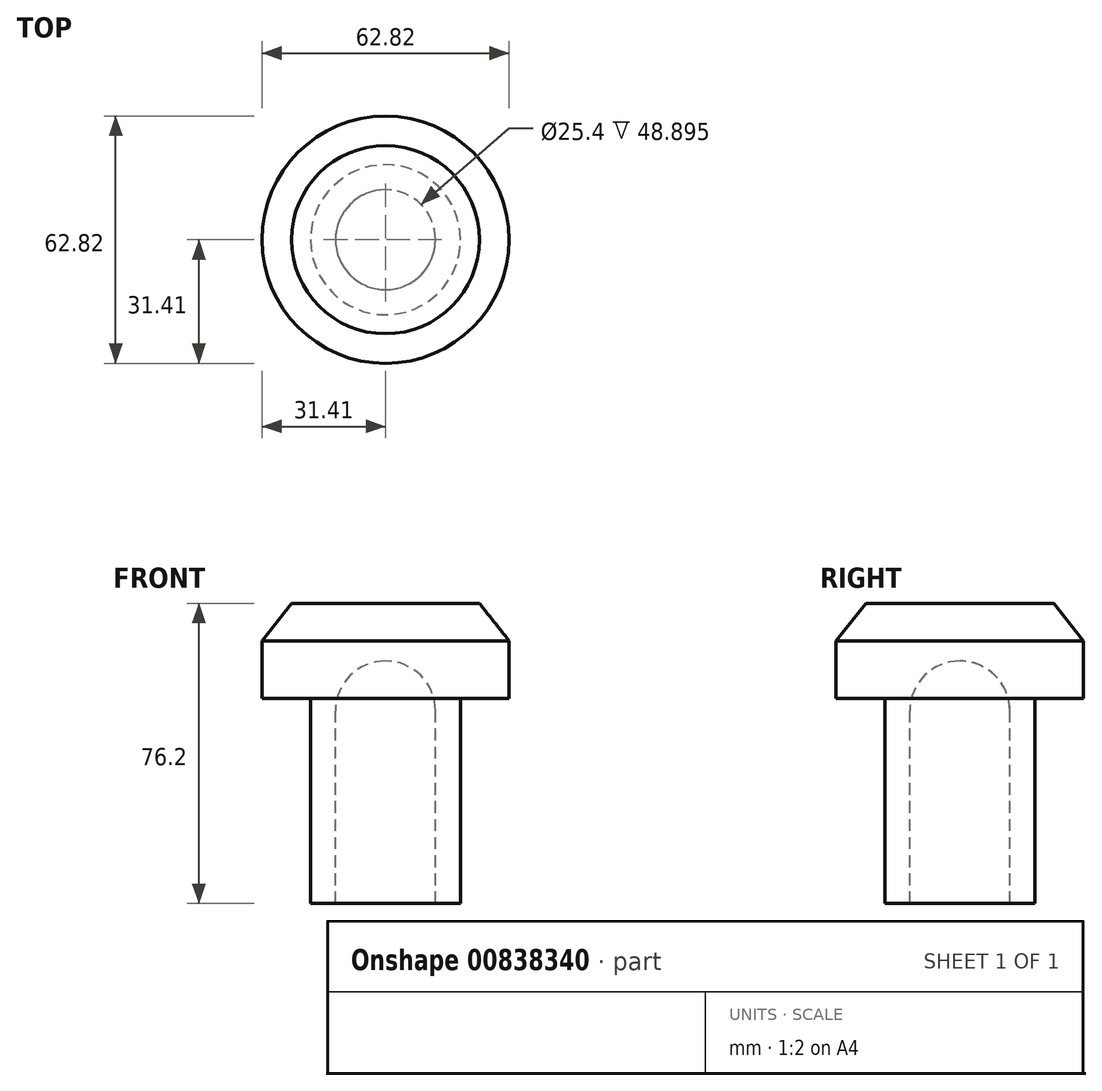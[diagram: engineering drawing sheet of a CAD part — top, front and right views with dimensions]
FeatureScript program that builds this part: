
annotation { "Feature Type Name" : "Feature", "Feature Type Description" : "" }
export const myFeature = defineFeature(function(context is Context, id is Id, definition is map)
    precondition{}
    {
        {
            var Q0;
            Q0=qCreatedBy(makeId("Right.planeOp"),FACE);
            var sketch = newSketch(context, id + "F0", { "sketchPlane" : qUnion([Q0])});
            skLineSegment(sketch, "E0", {"start": v(0, 0) * mm, "end": v(-19.05, 0) * mm});
            skLineSegment(sketch, "E1", {"start": v(-19.05, 0) * mm, "end": v(-19.05, 52.07) * mm});
            skLineSegment(sketch, "E2", {"start": v(-19.05, 52.07) * mm, "end": v(-31.4, 52.07) * mm});
            skLineSegment(sketch, "E3", {"start": v(-31.4, 52.07) * mm, "end": v(-31.4, 66.67) * mm});
            skLineSegment(sketch, "E4", {"start": v(-31.4, 66.67) * mm, "end": v(-23.87, 76.2) * mm});
            skLineSegment(sketch, "E5", {"start": v(-23.87, 76.2) * mm, "end": v(0, 76.2) * mm});
            skLineSegment(sketch, "E6", {"start": v(0, 76.2) * mm, "end": v(0, 61.6) * mm});
            skLineSegment(sketch, "E7", {"start": v(-12.7, 0) * mm, "end": v(-12.7, 48.9) * mm});
            skArc(sketch, "E8", {"start": v(0, 61.6) * mm, "mid": v(-8.98, 57.88) * mm, "end": v(-12.7, 48.9) * mm});
            skPoint(sketch, "E9.start.orphan", {"position": v(3.43, 61.6) * mm});
            skLineSegment(sketch, "E10.trimOffspring", {"start": v(0, 48.9) * mm, "end": v(0, 0) * mm});
            skSolve(sketch);
        }
        {
            var Q0;
            {var subQ0=sQuery(id+"F0.wireOp",EDGE,"E1");Q0=makeQuery(id+"F0.imprint","IMPRINT",FACE,{"disambiguationData":[TD([[makeQuery(id+"F0.imprint","IMPRINT",EDGE,{"derivedFrom":subQ0}),-1.0]])]});}
            var Q1;
            Q1=sQuery(id+"F0.wireOp",EDGE,"E6");
            revolve(context, id + "F1", {"surfaceOperationType" : NewSurfaceOperationType.NEW, "entities" : qUnion([Q0]), "axis" : qUnion([Q1]), "revolveType" : RevolveType.FULL});
        }
    });
